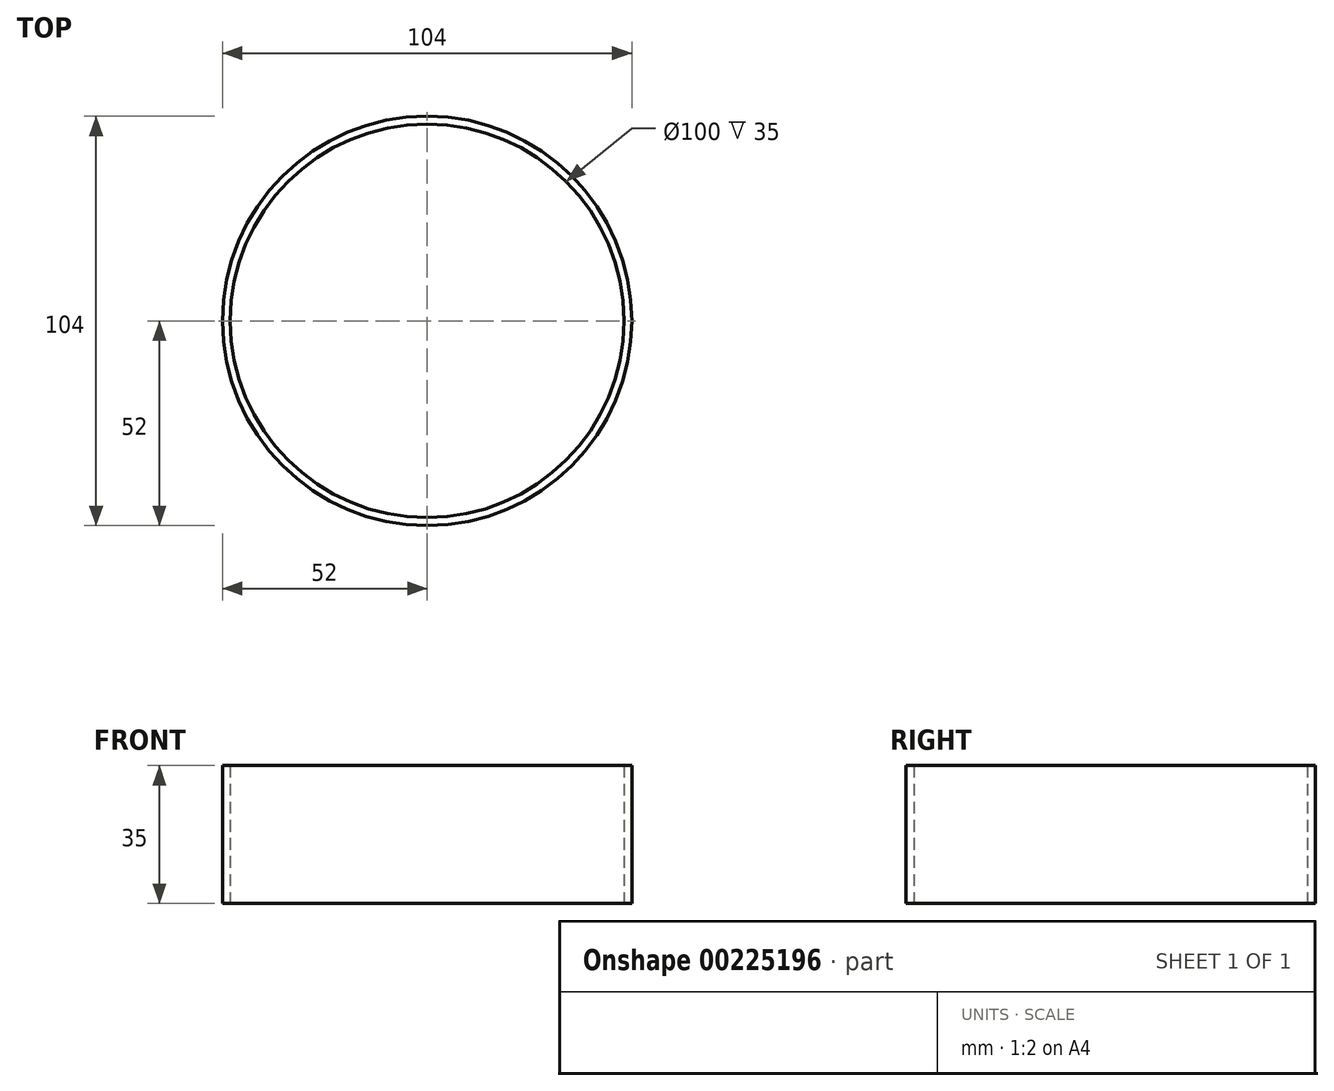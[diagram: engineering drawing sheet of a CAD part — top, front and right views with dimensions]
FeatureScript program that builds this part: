
annotation { "Feature Type Name" : "Feature", "Feature Type Description" : "" }
export const myFeature = defineFeature(function(context is Context, id is Id, definition is map)
    precondition{}
    {
        {
            var Q0;
            Q0=qCreatedBy(makeId("Top.planeOp"),FACE);
            var sketch = newSketch(context, id + "F0", { "sketchPlane" : qUnion([Q0])});
            skCircle(sketch, "E0", {"center": v(0, 0) * mm, "radius": 50 * mm});
            skCircle(sketch, "E1", {"center": v(0, 0) * mm, "radius": 52 * mm});
            skSolve(sketch);
        }
        {
            var Q0;
            Q0=makeQuery(id+"F0.imprint","IMPRINT",FACE,{"disambiguationData":[TD([[makeQuery(id+"F0.imprint","IMPRINT",EDGE,{"derivedFrom":sQuery(id+"F0.wireOp",EDGE,"E0")}),-1.0]])]});
            extrude(context, id + "F1", {"entities" : qUnion([Q0]), "depth" : 35 * mm});
        }
    });
